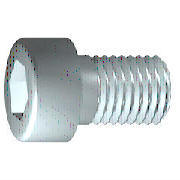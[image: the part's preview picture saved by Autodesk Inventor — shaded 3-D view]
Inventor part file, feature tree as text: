
AUTODESK INVENTOR PART (.ipt)
format: ipt  version: 2020 (Build 240168000, 168)  size: 190,464 bytes
history: native  units: mm (DEFAULTED — no unit token found)
features: sketch x2, other x1, extrude x1, plane x1, fillet x1
ambient origin geometry x7: Origin, YZ Plane, XY Plane, X Axis, Y Axis, Z Axis, Center Point
bodies: Solid1 (feature_tree)
feature tree (6):
  other  "Bryła"
  extrude  "Szczelina"  Depth=24.0mm
  plane  "Work Plane1"
  fillet  "Fillet2"  Radius=0.61355mm
  sketch  "Szkic1"
  sketch  "Szkic2"
